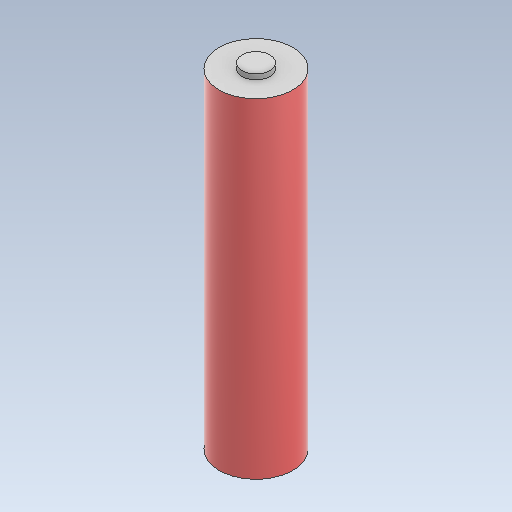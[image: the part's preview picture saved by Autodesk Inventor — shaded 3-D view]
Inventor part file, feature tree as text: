
AUTODESK INVENTOR PART (.ipt)
format: ipt  version: 2020 (Build 240168000, 168)  size: 108,544 bytes
history: native  units: mm
features: sketch x3, other x2, extrude x2
ambient origin geometry x8: Origin, YZ Plane, XZ Plane, XY Plane, X Axis, Y Axis, Z Axis, Center Point
bodies: Body1 (feature_tree)
feature tree (7):
  other  "Sólido1"
  extrude  "Extrusión1"  Depth=64.4mm TaperAngle=0.0deg
  extrude  "Extrusión2"  Depth=1.0mm TaperAngle=0.0deg
  sketch  "Boceto3"
  other  "Eje de trabajo1"
  sketch  "Boceto1"  dims[d0=14.4mm d1=64.4mm d2=0.0mm]
  sketch  "Boceto2"  dims[d3=5.4mm d4=1.0mm d5=0.0mm]
